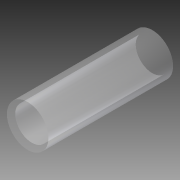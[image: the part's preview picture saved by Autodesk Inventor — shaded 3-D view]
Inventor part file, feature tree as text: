
AUTODESK INVENTOR PART (.ipt)
format: ipt  version: 2015 (Build 190159000, 159)  size: 88,064 bytes
history: native  units: mm
features: extrude x2, sketch x2
ambient origin geometry x8: Origin, YZ Plane, XZ Plane, XY Plane, X Axis, Y Axis, Z Axis, Center Point
bodies: Solid1 (feature_tree)
feature tree (4):
  extrude  "Extrusion1"  Depth=56.0mm
  extrude  "Extrusion2"  Depth=7.0mm TaperAngle=0.0deg
  sketch  "Sketch1"  dims[d0=70.0mm d1=56.0mm]
  sketch  "Sketch2"  dims[d2=210.0mm d3=0.0mm d4=7.0mm d5=0.0mm]
